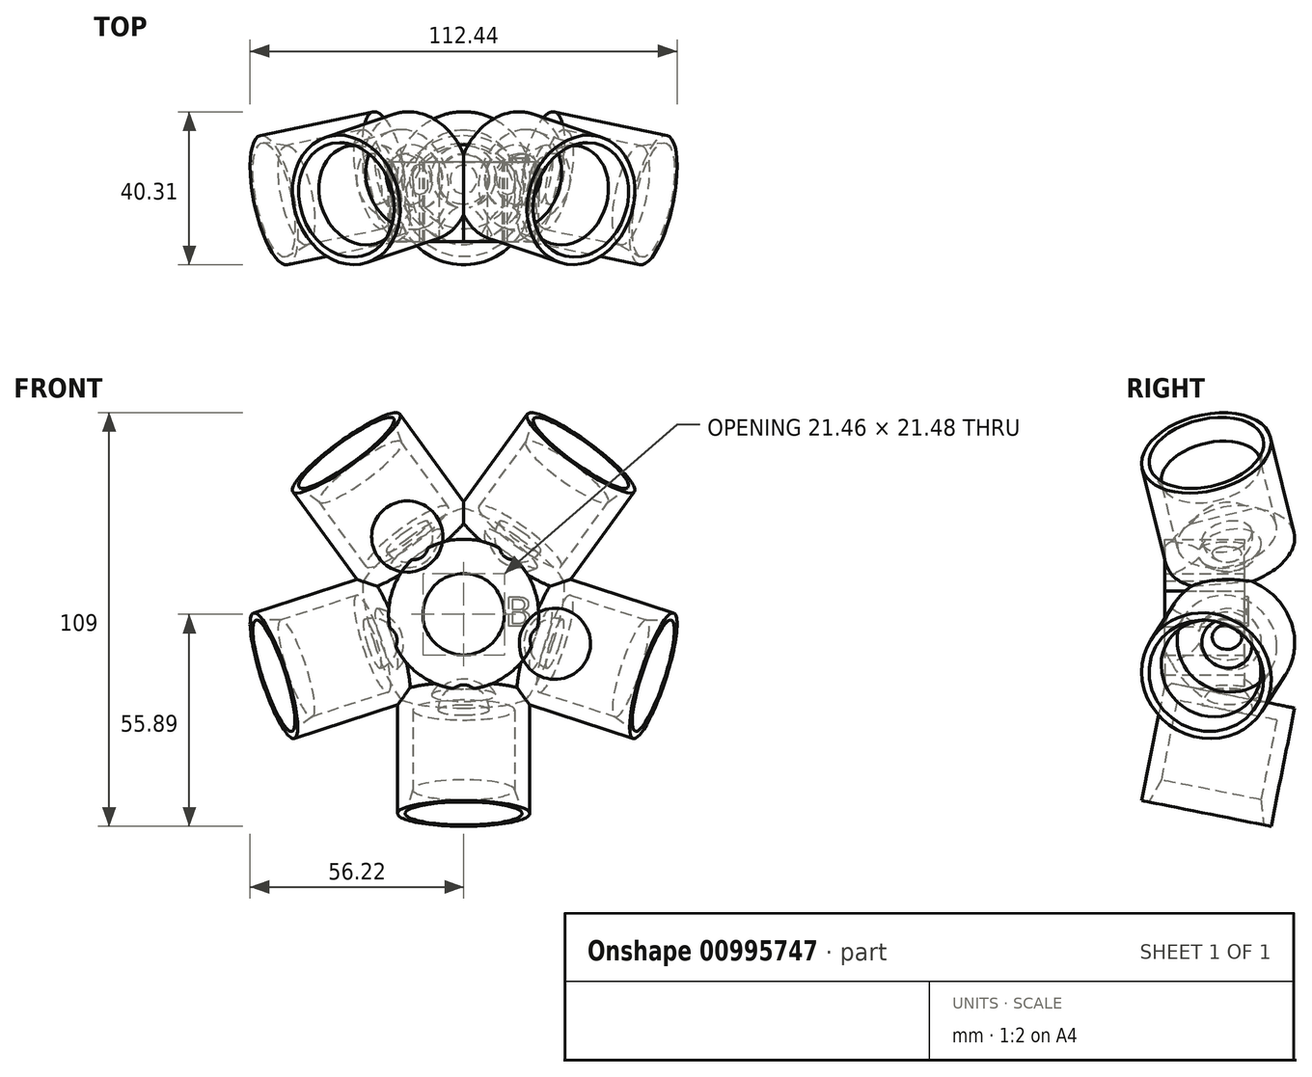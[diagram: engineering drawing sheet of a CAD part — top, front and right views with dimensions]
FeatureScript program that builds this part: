
annotation { "Feature Type Name" : "Feature", "Feature Type Description" : "" }
export const myFeature = defineFeature(function(context is Context, id is Id, definition is map)
    precondition{}
    {
        {
            var Q0;
            Q0=qCreatedBy(makeId("Front.planeOp"),FACE);
            var sketch = newSketch(context, id + "F0", { "sketchPlane" : qUnion([Q0])});
            skPoint(sketch, "E0.middle", {"position": v(0, 0) * mm});
            skPoint(sketch, "E1", {"position": v(0, 41.61) * mm});
            skCircle(sketch, "E2", {"center": v(0, 41.61) * mm, "radius": 19.5 * mm});
            skCircle(sketch, "E3", {"center": v(0, 41.61) * mm, "radius": 11 * mm});
            skLineSegment(sketch, "E4", {"start": v(0, 75.85) * mm, "end": v(0, -7.97) * mm, "construction": true});
            skPoint(sketch, "E5", {"position": v(0, 19.61) * mm});
            skLineSegment(sketch, "E6", {"start": v(26.39, 19.61) * mm, "end": v(-30.99, 19.61) * mm, "construction": true});
            skText(sketch, "E7", { "text": "B", "fontName": "OpenSans-Regular.ttf"});
            const initialGuessF0  = {"E7": [0.01089, 0.03873, 1, 0, 0.00777]};
            skSetInitialGuess(sketch, initialGuessF0);
            skSolve(sketch);
        }
        {
            var Q0;
            Q0=sQuery(id+"F0.wireOp",EDGE,"E6");
            cPlane(context, id + "F1", {"entities" : qUnion([Q0]), "cplaneType" : CPlaneType.LINE_ANGLE, "offset" : 25 * mm, "angle" : 11.25 * degree, "width" : 150 * mm, "height" : 150 * mm});
        }
        {
            var Q0;
            Q0=qCreatedBy(id+"F1.planeOp",FACE);
            var sketch = newSketch(context, id + "F2", { "sketchPlane" : qUnion([Q0])});
            skPoint(sketch, "E8", {"position": v(-6.69, 29.59) * mm});
            skLineSegment(sketch, "E9.right", {"start": v(13.39, 16.2) * mm, "end": v(13.39, -5.25) * mm});
            skArc(sketch, "E10", {"start": v(6.73, 16.2) * mm, "mid": v(4.76, 20.95) * mm, "end": v(0, 22.92) * mm});
            skArc(sketch, "E11", {"start": v(8.47, 20.2) * mm, "mid": v(5.01, 24.1) * mm, "end": v(0, 25.56) * mm});
            skLineSegment(sketch, "E12", {"start": v(17.39, 20.2) * mm, "end": v(17.39, -11.6) * mm});
            skLineSegment(sketch, "E13", {"start": v(15.39, -11.6) * mm, "end": v(17.39, -11.6) * mm});
            skLineSegment(sketch, "E14", {"start": v(17.39, 20.2) * mm, "end": v(8.47, 20.2) * mm});
            skLineSegment(sketch, "E15", {"start": v(15.39, -11.6) * mm, "end": v(13.39, -5.25) * mm});
            skLineSegment(sketch, "E16", {"start": v(13.39, 16.2) * mm, "end": v(6.73, 16.2) * mm});
            skLineSegment(sketch, "E17", {"start": v(0, 22.92) * mm, "end": v(0, 25.56) * mm});
            skSolve(sketch);
        }
        {
            var Q0;
            Q0=makeQuery(id+"F2.imprint","IMPRINT",FACE,{"disambiguationData":[TD([[makeQuery(id+"F2.imprint","IMPRINT",EDGE,{"derivedFrom":sQuery(id+"F2.wireOp",EDGE,"E9.right")}),1.0]])]});
            var Q1;
            Q1=sQuery(id+"F2.wireOp",EDGE,"E17");
            revolve(context, id + "F3", {"surfaceOperationType" : NewSurfaceOperationType.NEW, "entities" : qUnion([Q0]), "axis" : qUnion([Q1]), "revolveType" : RevolveType.FULL});
        }
        {
            var Q0;
            Q0=makeQuery(id+"F0.imprint","IMPRINT",FACE,{"disambiguationData":[TD([[makeQuery(id+"F0.imprint","IMPRINT",EDGE,{"derivedFrom":sQuery(id+"F0.wireOp",EDGE,"E2")}),1.0]])]});
            extrude(context, id + "F4", {"entities" : qUnion([Q0]), "operationType" : NewBodyOperationType.ADD, "depth" : 17 * mm, "offsetDistance" : 25 * mm, "hasSecondDirection" : true, "secondDirectionOppositeDirection" : true, "secondDirectionDepth" : 4 * mm});
        }
        {
            var Q0;
            Q0=qCreatedBy(makeId("Right.planeOp"),FACE);
            var sketch = newSketch(context, id + "F5", { "sketchPlane" : qUnion([Q0])});
            skLineSegment(sketch, "E18", {"start": v(-35.17, 41.9) * mm, "end": v(25.33, 41.9) * mm, "construction": true});
            skSolve(sketch);
        }
        {
            var Q0;
            Q0=makeQuery(id+"F3.opRevolve","SWEPT_BODY",BODY,{"disambiguationData":[OSD([sQuery(id+"F2.wireOp",EDGE,"E9.right"),sQuery(id+"F2.wireOp",EDGE,"E10"),sQuery(id+"F2.wireOp",EDGE,"E11"),sQuery(id+"F2.wireOp",EDGE,"E12"),sQuery(id+"F2.wireOp",EDGE,"E13"),sQuery(id+"F2.wireOp",EDGE,"E14"),sQuery(id+"F2.wireOp",EDGE,"E15"),sQuery(id+"F2.wireOp",EDGE,"E16"),sQuery(id+"F2.wireOp",EDGE,"E17")])]});
            var Q1;
            Q1=sQuery(id+"F5.wireOp",EDGE,"E18");
            circularPattern(context, id + "F6", {"entities" : qUnion([Q0]), "axis" : qUnion([Q1]), "angle" : 360 * degree, "instanceCount" : 5, "equalSpace" : true});
        }
        {
            var Q0;
            Q0=makeQuery(id+"F0.imprint","IMPRINT",FACE,{"disambiguationData":[TD([[makeQuery(id+"F0.imprint","IMPRINT",EDGE,{"derivedFrom":sQuery(id+"F0.wireOp",EDGE,"E7.sketch_text.stroke-0")}),-1.0]])]});
            extrude(context, id + "F7", {"entities" : qUnion([Q0]), "operationType" : NewBodyOperationType.ADD, "oppositeDirection" : true, "depth" : 5 * mm, "offsetDistance" : 25 * mm});
        }
    });
